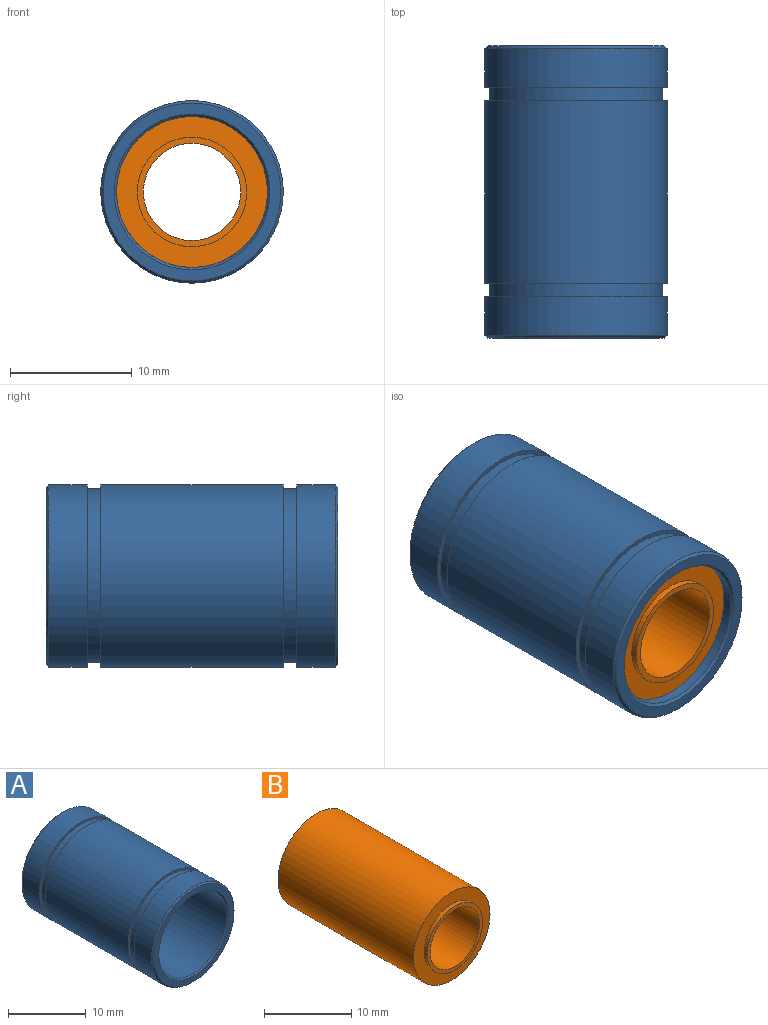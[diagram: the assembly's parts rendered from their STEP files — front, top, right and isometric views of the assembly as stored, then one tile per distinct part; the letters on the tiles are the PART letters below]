
ASSEMBLY  parts=2 mates=1
PART A: 16 faces, bbox 15x24x15 mm
  f0: cylinder r=7.5mm len=15mm, axis (0,1,0), area 150.8mm2, adj f6,f9
  f1: cylinder r=6.2mm len=23.6mm, axis (0,1,0), area 919.4mm2, adj f5,f7
  f2: cylinder r=7.5mm len=15mm, axis (0,1,0), area 150.8mm2, adj f8,f12
  f3: plane 14.6x14.6mm, normal (0,-1,0), area 38.7mm2, adj f7,f8
  f4: plane 14.6x14.6mm, normal (0,1,0), area 38.7mm2, adj f5,f6
  f5: cone r=6.4mm half-angle=45deg, axis (0,1,0), area 11.2mm2, adj f1,f4
  f6: cone r=7.5mm half-angle=45deg, axis (0,-1,0), area 13.2mm2, adj f0,f4
  f7: cone r=6.2mm half-angle=45deg, axis (0,-1,0), area 11.2mm2, adj f1,f3
  f8: cone r=7.3mm half-angle=45deg, axis (0,1,0), area 13.2mm2, adj f2,f3
  f9: plane 15x15mm, normal (0,-1,0), area 16.1mm2, adj f0,f11
  f10: plane 15x15mm, normal (0,1,0), area 16.1mm2, adj f11,f15
  f11: cylinder r=7.15mm len=14.3mm, axis (0,1,0), area 49.4mm2, adj f9,f10
  f12: plane 15x15mm, normal (0,1,0), area 16.1mm2, adj f2,f14
  f13: plane 15x15mm, normal (0,-1,0), area 16.1mm2, adj f14,f15
  f14: cylinder r=7.15mm len=14.3mm, axis (0,1,0), area 49.4mm2, adj f12,f13
  f15: cylinder r=7.5mm len=15mm, axis (0,1,0), area 706.9mm2, adj f10,f13
PART B: 8 faces, bbox 12.4x23x12.4 mm
  f0: cylinder r=6.2mm len=22mm, axis (0,1,0), area 857mm2, adj f1,f2
  f1: plane 12.4x12.4mm, normal (0,-1,0), area 57.1mm2, adj f0,f3
  f2: plane 12.4x12.4mm, normal (0,1,0), area 57.1mm2, adj f0,f5
  f3: cylinder r=4.5mm len=9mm, axis (0,1,0), area 14.1mm2, adj f1,f6
  f4: cylinder r=4mm len=23mm, axis (0,1,0), area 578.1mm2, adj f6,f7
  f5: cylinder r=4.5mm len=9mm, axis (0,1,0), area 14.1mm2, adj f2,f7
  f6: plane 9x9mm, normal (0,-1,0), area 13.4mm2, adj f3,f4
  f7: plane 9x9mm, normal (0,1,0), area 13.4mm2, adj f4,f5
PLACE A t=(11.4,-7.41,-3.16)mm
PLACE B t=(11.4,-7.41,-3.16)mm
MATE fastened B.f0 <-> A.f0  axis (0,1,0) through (11.4,-7.41,-3.16)mm
